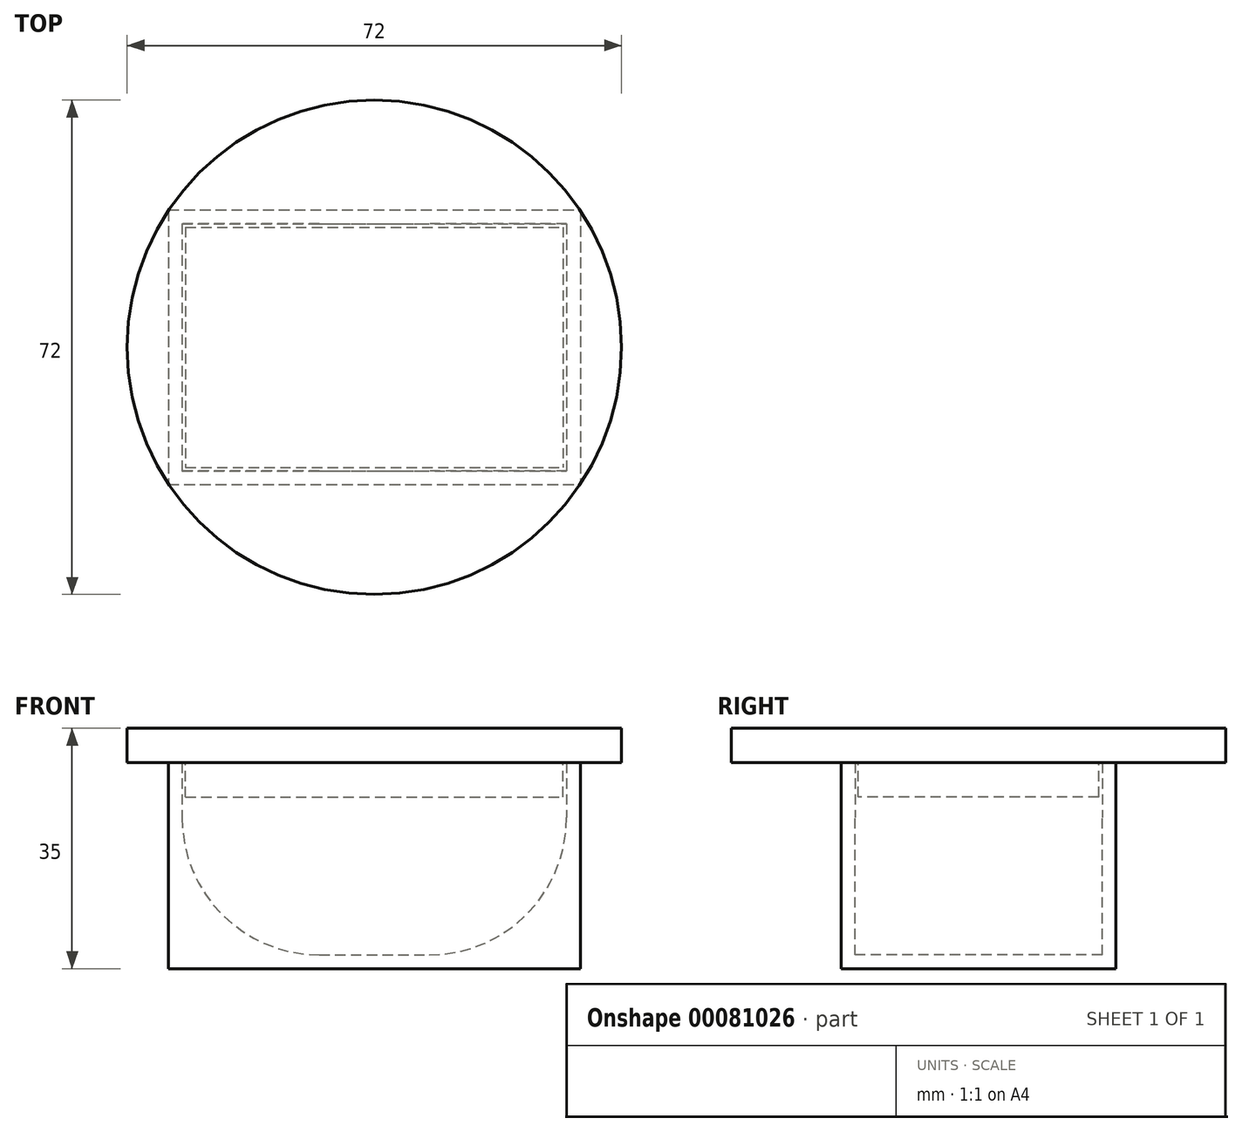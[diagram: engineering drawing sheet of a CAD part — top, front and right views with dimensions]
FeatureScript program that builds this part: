
annotation { "Feature Type Name" : "Feature", "Feature Type Description" : "" }
export const myFeature = defineFeature(function(context is Context, id is Id, definition is map)
    precondition{}
    {
        {
            var Q0;
            Q0=qCreatedBy(makeId("Top.planeOp"),FACE);
            var sketch = newSketch(context, id + "F0", { "sketchPlane" : qUnion([Q0])});
            skLineSegment(sketch, "E0.bottom", {"start": v(-30, 20) * mm, "end": v(30, 20) * mm});
            skLineSegment(sketch, "E0.top", {"start": v(-30, -20) * mm, "end": v(30, -20) * mm});
            skLineSegment(sketch, "E0.left", {"start": v(-30, 20) * mm, "end": v(-30, -20) * mm});
            skLineSegment(sketch, "E0.right", {"start": v(30, 20) * mm, "end": v(30, -20) * mm});
            skPoint(sketch, "E0.middle", {"position": v(0, 0) * mm});
            skSolve(sketch);
        }
        {
            var Q0;
            Q0=makeQuery(id+"F0.imprint","IMPRINT",FACE,{"disambiguationData":[TD([[makeQuery(id+"F0.imprint","IMPRINT",EDGE,{"derivedFrom":sQuery(id+"F0.wireOp",EDGE,"E0.bottom")}),-1.0]])]});
            extrude(context, id + "F1", {"entities" : qUnion([Q0]), "depth" : 30 * mm});
        }
        {
            var Q0;
            Q0=makeQuery(id+"F1.opExtrude","CAP_FACE",FACE,{"disambiguationData":[OSD([sQuery(id+"F0.wireOp",EDGE,"E0.bottom"),sQuery(id+"F0.wireOp",EDGE,"E0.top"),sQuery(id+"F0.wireOp",EDGE,"E0.left"),sQuery(id+"F0.wireOp",EDGE,"E0.right")])],"isStart":false});
            shell(context, id + "F2", {"entities" : qUnion([Q0]), "thickness" : 2 * mm});
        }
        {
            var Q0;
            {var subQ0=sQuery(id+"F0.wireOp",EDGE,"E0.right");Q0=makeQuery(id+"F2.opShell","OFFSET_EDGE",EDGE,{"disambiguationData":[OSD([subQ0]),TDD([makeQuery(id+"F1.opExtrude","CAP_EDGE",EDGE,{"disambiguationData":[OSD([subQ0])],"isStart":true})])]});}
            var Q1;
            {var subQ0=sQuery(id+"F0.wireOp",EDGE,"E0.left");Q1=makeQuery(id+"F2.opShell","OFFSET_EDGE",EDGE,{"disambiguationData":[OSD([subQ0]),TDD([makeQuery(id+"F1.opExtrude","CAP_EDGE",EDGE,{"disambiguationData":[OSD([subQ0])],"isStart":true})])]});}
            fillet(context, id + "F3", {"entities" : qUnion([Q0, Q1]), "radius" : 20 * mm, "tangentPropagation" : true, "allowEdgeOverflow" : false});
        }
        {
            var Q0;
            Q0=makeQuery(id+"F1.opExtrude","CAP_FACE",FACE,{"disambiguationData":[OSD([sQuery(id+"F0.wireOp",EDGE,"E0.bottom"),sQuery(id+"F0.wireOp",EDGE,"E0.top"),sQuery(id+"F0.wireOp",EDGE,"E0.left"),sQuery(id+"F0.wireOp",EDGE,"E0.right")])],"isStart":false});
            var sketch = newSketch(context, id + "F4", { "sketchPlane" : qUnion([Q0])});
            skLineSegment(sketch, "E1.bottom", {"start": v(-27.5, 17.5) * mm, "end": v(27.5, 17.5) * mm});
            skLineSegment(sketch, "E1.top", {"start": v(-27.5, -17.5) * mm, "end": v(27.5, -17.5) * mm});
            skLineSegment(sketch, "E1.left", {"start": v(-27.5, 17.5) * mm, "end": v(-27.5, -17.5) * mm});
            skLineSegment(sketch, "E1.right", {"start": v(27.5, 17.5) * mm, "end": v(27.5, -17.5) * mm});
            skSolve(sketch);
        }
        {
            var Q0;
            Q0=makeQuery(id+"F4.imprint","IMPRINT",FACE,{"disambiguationData":[TD([[makeQuery(id+"F4.imprint","IMPRINT",EDGE,{"derivedFrom":sQuery(id+"F4.wireOp",EDGE,"E1.bottom")}),-1.0]])]});
            extrude(context, id + "F5", {"entities" : qUnion([Q0]), "oppositeDirection" : true, "depth" : 5 * mm});
        }
        {
            var Q0;
            Q0=makeQuery(id+"F5.opExtrude","CAP_FACE",FACE,{"disambiguationData":[OSD([sQuery(id+"F4.wireOp",EDGE,"E1.bottom"),sQuery(id+"F4.wireOp",EDGE,"E1.top"),sQuery(id+"F4.wireOp",EDGE,"E1.left"),sQuery(id+"F4.wireOp",EDGE,"E1.right")])],"isStart":true});
            var sketch = newSketch(context, id + "F6", { "sketchPlane" : qUnion([Q0])});
            skCircle(sketch, "E2", {"center": v(0, 0) * mm, "radius": 36 * mm});
            skSolve(sketch);
        }
        {
            var Q0;
            Q0=makeQuery(id+"F6.imprint","IMPRINT",FACE,{"disambiguationData":[TD([[makeQuery(id+"F6.imprint","IMPRINT",EDGE,{"derivedFrom":sQuery(id+"F6.wireOp",EDGE,"E2")}),1.0]])]});
            var Q1;
            Q1=makeQuery(id+"F6.imprint","IMPRINT",FACE,{"disambiguationData":[TD([[makeQuery(id+"F6.imprint","IMPRINT",EDGE,{"derivedFrom":makeQuery(id+"F5.opExtrude","CAP_EDGE",EDGE,{"disambiguationData":[OSD([sQuery(id+"F4.wireOp",EDGE,"E1.bottom")])],"isStart":true})}),-1.0]])]});
            extrude(context, id + "F7", {"entities" : qUnion([Q0, Q1]), "depth" : 5 * mm});
        }
    });
